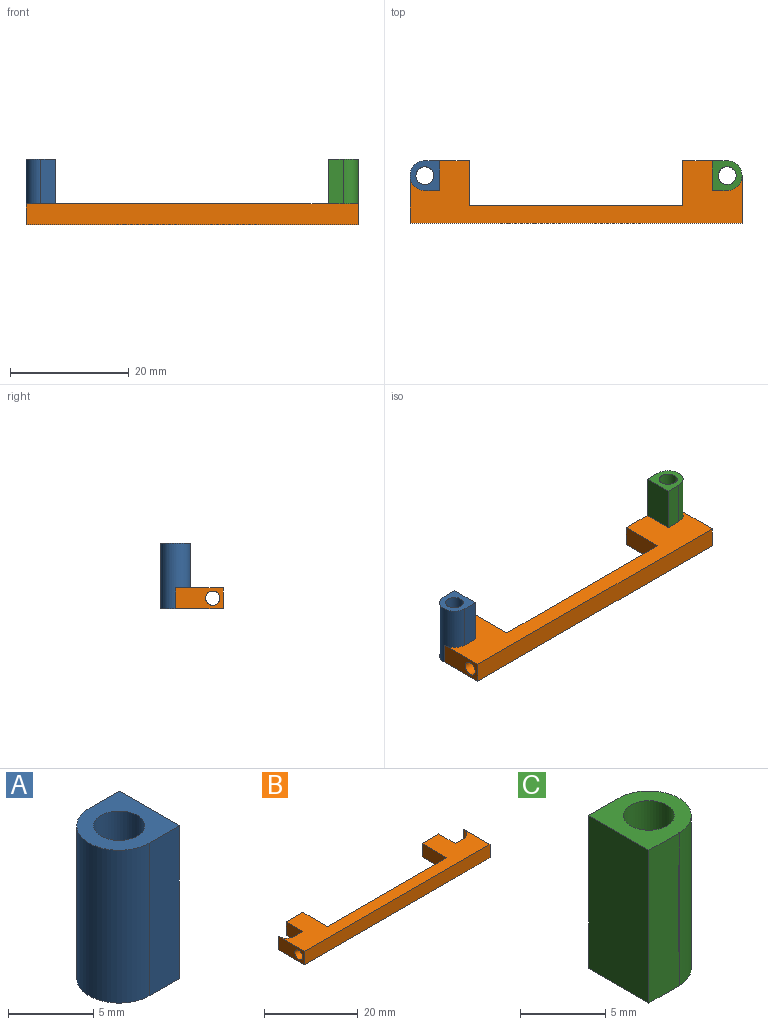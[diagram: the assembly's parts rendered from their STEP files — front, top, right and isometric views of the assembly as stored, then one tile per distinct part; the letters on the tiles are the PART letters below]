
ASSEMBLY  parts=3 mates=2
PART A: 7 faces, bbox 5x5x11 mm
  f0: plane 11x2.5mm, normal (0,1,0), area 27.5mm2, adj f1,f4,f5,f6
  f1: cylinder r=2.5mm len=11mm, axis (0,0,-1), area 86.4mm2, adj f0,f2,f5,f6
  f2: plane 11x2.5mm, normal (0,-1,0), area 27.5mm2, adj f1,f4,f5,f6
  f3: cylinder r=1.5mm len=11mm, axis (0,0,-1), area 103.7mm2, adj f5,f6
  f4: plane 11x5mm, normal (1,0,0), area 55mm2, adj f0,f2,f5,f6
  f5: plane 5x5mm, normal (0,0,1), area 15.2mm2, adj f0,f1,f2,f3,f4
  f6: plane 5x5mm, normal (0,0,-1), area 15.2mm2, adj f0,f1,f2,f3,f4
PART B: 18 faces, bbox 56x10.5x3.5 mm
  f0: plane 8x3.5mm, normal (1,0,0), area 23.5mm2, adj f1,f14,f15,f16,f17
  f1: cylinder r=2.5mm len=3.5mm, axis (0,0,-1), area 13.7mm2, adj f0,f2,f15,f16
  f2: plane 3.5x0.01mm, normal (-1,0,0), area 0mm2, adj f1,f3,f15,f16
  f3: plane 3.5x2.5mm, normal (0,1,0), area 8.7mm2, adj f2,f4,f15,f16
  f4: plane 5.01x3.5mm, normal (1,0,0), area 17.5mm2, adj f3,f5,f15,f16
  f5: plane 5x3.5mm, normal (0,1,0), area 17.5mm2, adj f4,f6,f15,f16
  f6: plane 7.5x3.5mm, normal (-1,0,0), area 26.3mm2, adj f5,f7,f15,f16
  f7: plane 36x3.5mm, normal (0,1,0), area 126mm2, adj f6,f8,f15,f16
  f8: plane 7.5x3.5mm, normal (1,0,0), area 26.3mm2, adj f7,f9,f15,f16
  f9: plane 5x3.5mm, normal (0,1,0), area 17.5mm2, adj f8,f10,f15,f16
  f10: plane 5x3.5mm, normal (-1,0,0), area 17.5mm2, adj f9,f11,f15,f16
  f11: plane 3.5x2.5mm, normal (0,1,0), area 8.8mm2, adj f10,f12,f15,f16
  f12: cylinder r=2.5mm len=3.5mm, axis (0,0,-1), area 13.7mm2, adj f11,f13,f15,f16
  f13: plane 8x3.5mm, normal (-1,0,0), area 23.5mm2, adj f12,f14,f15,f16,f17
  f14: plane 56x3.5mm, normal (0,-1,0), area 196mm2, adj f0,f13,f15,f16
  f15: plane 56x10.5mm, normal (0,0,1), area 270.7mm2, adj f0,f1,f2,f3,f4,f5,f6,f7
  f16: plane 56x10.5mm, normal (0,0,-1), area 270.7mm2, adj f0,f1,f2,f3,f4,f5,f6,f7
  f17: cylinder r=1.2mm len=56mm, axis (-1,0,0), area 422.2mm2, adj f0,f13
PART C: 8 faces, bbox 5x5x11 mm
  f0: cylinder r=2.5mm len=11mm, axis (0,0,-1), area 86.4mm2, adj f1,f5,f6,f7
  f1: plane 11x2.5mm, normal (0,1,0), area 27.5mm2, adj f0,f2,f6,f7
  f2: plane 11x5.01mm, normal (-1,0,0), area 55.1mm2, adj f1,f3,f6,f7
  f3: plane 11x2.5mm, normal (0,-1,0), area 27.5mm2, adj f2,f5,f6,f7
  f4: cylinder r=1.5mm len=11mm, axis (0,0,-1), area 103.7mm2, adj f6,f7
  f5: plane 11x0.01mm, normal (1,0,0), area 0.1mm2, adj f0,f3,f6,f7
  f6: plane 5.01x5mm, normal (0,0,1), area 15.3mm2, adj f0,f1,f2,f3,f4,f5
  f7: plane 5.01x5mm, normal (0,0,-1), area 15.3mm2, adj f0,f1,f2,f3,f4,f5
PLACE A t=(25.36,22.91,4.27)mm
PLACE B t=(25.36,22.91,4.27)mm
PLACE C t=(25.36,22.91,4.27)mm
MATE fastened C.f4 <-> B.f1  axis (0,0,-1) through (76.36,22.91,4.27)mm
MATE fastened B.f12 <-> A.f3  axis (0,0,-1) through (25.36,22.91,4.27)mm
